# Revit family: S350
name_source: partatom
category: Modelos genéricos
revit_build: Autodesk Revit 2017 (Build: 20170118_1100(x64)
units: mm (PartAtom-declared; Revit-internal decimal feet)

## family parameters
Compartido = No
Corte con vacíos al cargar = No
Cota de conector redondo = Diámetro de uso
Puede alojar armadura = No
Punto de cálculo de habitación = No
Tipo de pieza = Normal

## types (4) — shared parameters
Anchura exterior = 360 mm  [stored 1.1811 ft]
Anchura interior = 300 mm
Clase de carga = F-900 Norma EN-1433
Fabricante = ULMA Architectural
Ficha técnica = http://www.ulmaarchitectural.com
Pendiente = 0.00%
URL = http://www.ulmaarchitectural.com
Ø salida horizontal = 0 mm

## per-type parameters (varying)
| type | Altura | Caudal de referencia | Costo | Descripción | Peso | Sección hidráulica | Ø salida vertical |
| S350F | 210 mm  [stored 0.688976 ft] | 23 L/s | 107.54€ | Canal de Hormigón Polímero tipo ULMA / modelo S350F / ancho exterior 360mm / ancho interior 300mm y con altura exterior de 210mm / para recogida de aguas pluviales / en módulos de 1 ML de longitud / fijación de seguridad en 8 puntos por ML / perfiles de acero galvanizado* para protección lateral. | 43.37 kg | 455.00 cm² | 250 mm |
| S350MF | 210 mm  [stored 0.688976 ft] | 23 L/s | 134.86€ | Canal de Hormigón Polímero tipo ULMA / modelo S350MF / ancho exterior 360mm / ancho interior 300mm y con altura exterior de 210mm / para recogida de aguas pluviales / en módulos de 1 ML de longitud / fijación de seguridad en 8 puntos por ML / perfiles de acero galvanizado* para protección lateral. | 45.03 kg | 455.00 cm² | 250 mm |
| SM350F | 150 mm  [stored 0.492126 ft] | 12 L/s | 106.77€ | Canal de Hormigón Polímero tipo ULMA / modelo SM350F / ancho exterior 360mm / ancho interior 300mm y con altura exterior de 150mm / para recogida de aguas pluviales / en módulos de 1 ML de longitud / fijación de seguridad en 8 puntos por ML / perfiles de acero galvanizado* para protección lateral. | 41.12 kg | 294.00 cm² | 200 mm |
| SM350MF | 150 mm  [stored 0.492126 ft] | 12 L/s | 126.34€ | Canal de Hormigón Polímero tipo ULMA / modelo SM350MF / ancho exterior 360mm / ancho interior 300mm y con altura exterior de 150mm / para recogida de aguas pluviales / en módulos de 1 ML de longitud / fijación de seguridad en 8 puntos por ML / perfiles de acero galvanizado* para protección lateral. | 42.78 kg | 294.00 cm² | 200 mm |

note: column(s) folded — value = type name in every type: Modelo

note: [stored X ft] marks values corroborated as IEEE doubles in the binary element streams (Revit-internal decimal feet)
